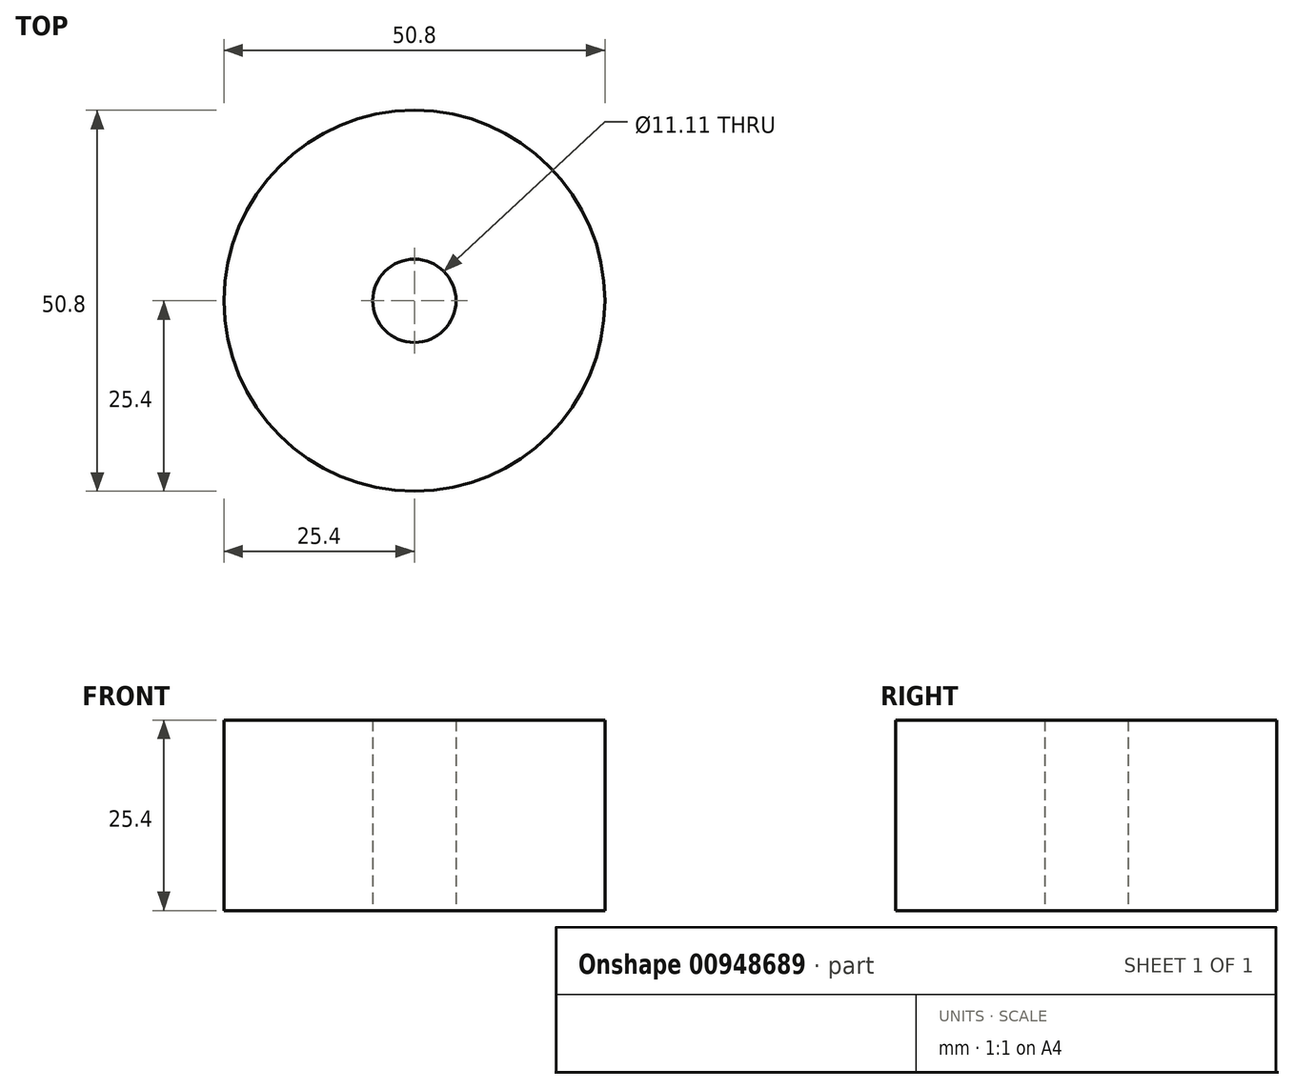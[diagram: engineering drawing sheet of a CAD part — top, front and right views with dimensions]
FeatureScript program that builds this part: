
annotation { "Feature Type Name" : "Feature", "Feature Type Description" : "" }
export const myFeature = defineFeature(function(context is Context, id is Id, definition is map)
    precondition{}
    {
        {
            var Q0;
            Q0=qCreatedBy(makeId("Top.planeOp"),FACE);
            var sketch = newSketch(context, id + "F0", { "sketchPlane" : qUnion([Q0])});
            skCircle(sketch, "E0", {"center": v(0, 0) * mm, "radius": 5.56 * mm});
            skCircle(sketch, "E1", {"center": v(0, 0) * mm, "radius": 25.4 * mm});
            skSolve(sketch);
        }
        {
            var Q0;
            Q0 = qSketchRegion(id + "F0", true);
            extrude(context, id + "F1", {"entities" : qUnion([Q0]), "depth" : 25.4 * mm, "offsetDistance" : 25.4 * mm});
        }
    });
